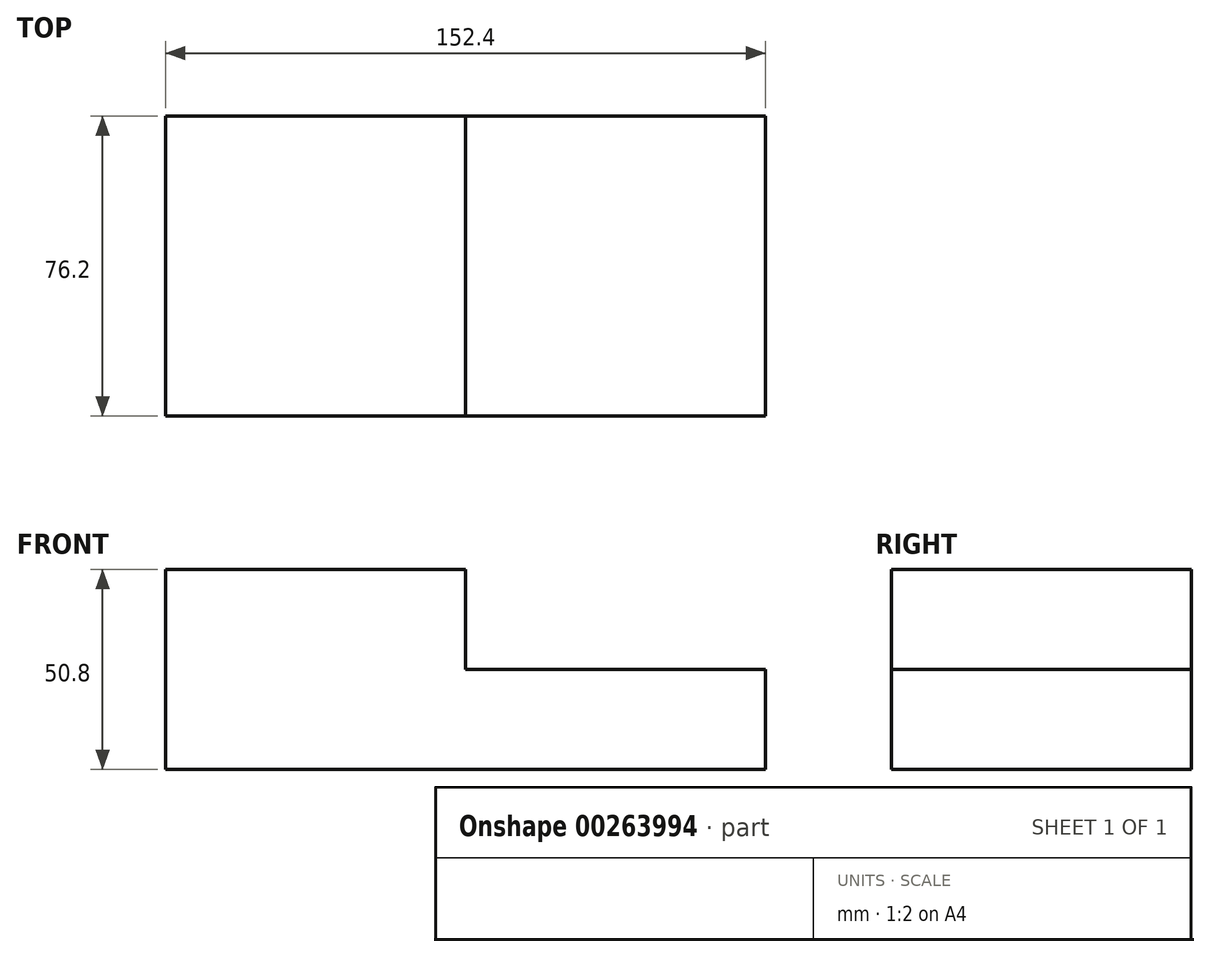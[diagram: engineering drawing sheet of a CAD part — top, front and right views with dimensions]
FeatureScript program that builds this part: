
annotation { "Feature Type Name" : "Feature", "Feature Type Description" : "" }
export const myFeature = defineFeature(function(context is Context, id is Id, definition is map)
    precondition{}
    {
        {
            var Q0;
            Q0=qCreatedBy(makeId("Front.planeOp"),FACE);
            var sketch = newSketch(context, id + "F0", { "sketchPlane" : qUnion([Q0])});
            skLineSegment(sketch, "E0", {"start": v(-76.2, 0) * mm, "end": v(0, 0) * mm});
            skLineSegment(sketch, "E1", {"start": v(0, 0) * mm, "end": v(0, -25.4) * mm});
            skLineSegment(sketch, "E2", {"start": v(0, -25.4) * mm, "end": v(76.2, -25.4) * mm});
            skLineSegment(sketch, "E3", {"start": v(-76.2, 0) * mm, "end": v(-76.2, -50.8) * mm});
            skLineSegment(sketch, "E4", {"start": v(-76.2, -50.8) * mm, "end": v(76.2, -50.8) * mm});
            skLineSegment(sketch, "E5", {"start": v(76.2, -25.4) * mm, "end": v(76.2, -50.8) * mm});
            skSolve(sketch);
        }
        {
            var Q0;
            Q0=makeQuery(id+"F0.imprint","IMPRINT",FACE,{"disambiguationData":[TD([[makeQuery(id+"F0.imprint","IMPRINT",EDGE,{"derivedFrom":sQuery(id+"F0.wireOp",EDGE,"E0")}),-1.0]])]});
            extrude(context, id + "F1", {"entities" : qUnion([Q0]), "depth" : 76.2 * mm});
        }
    });
